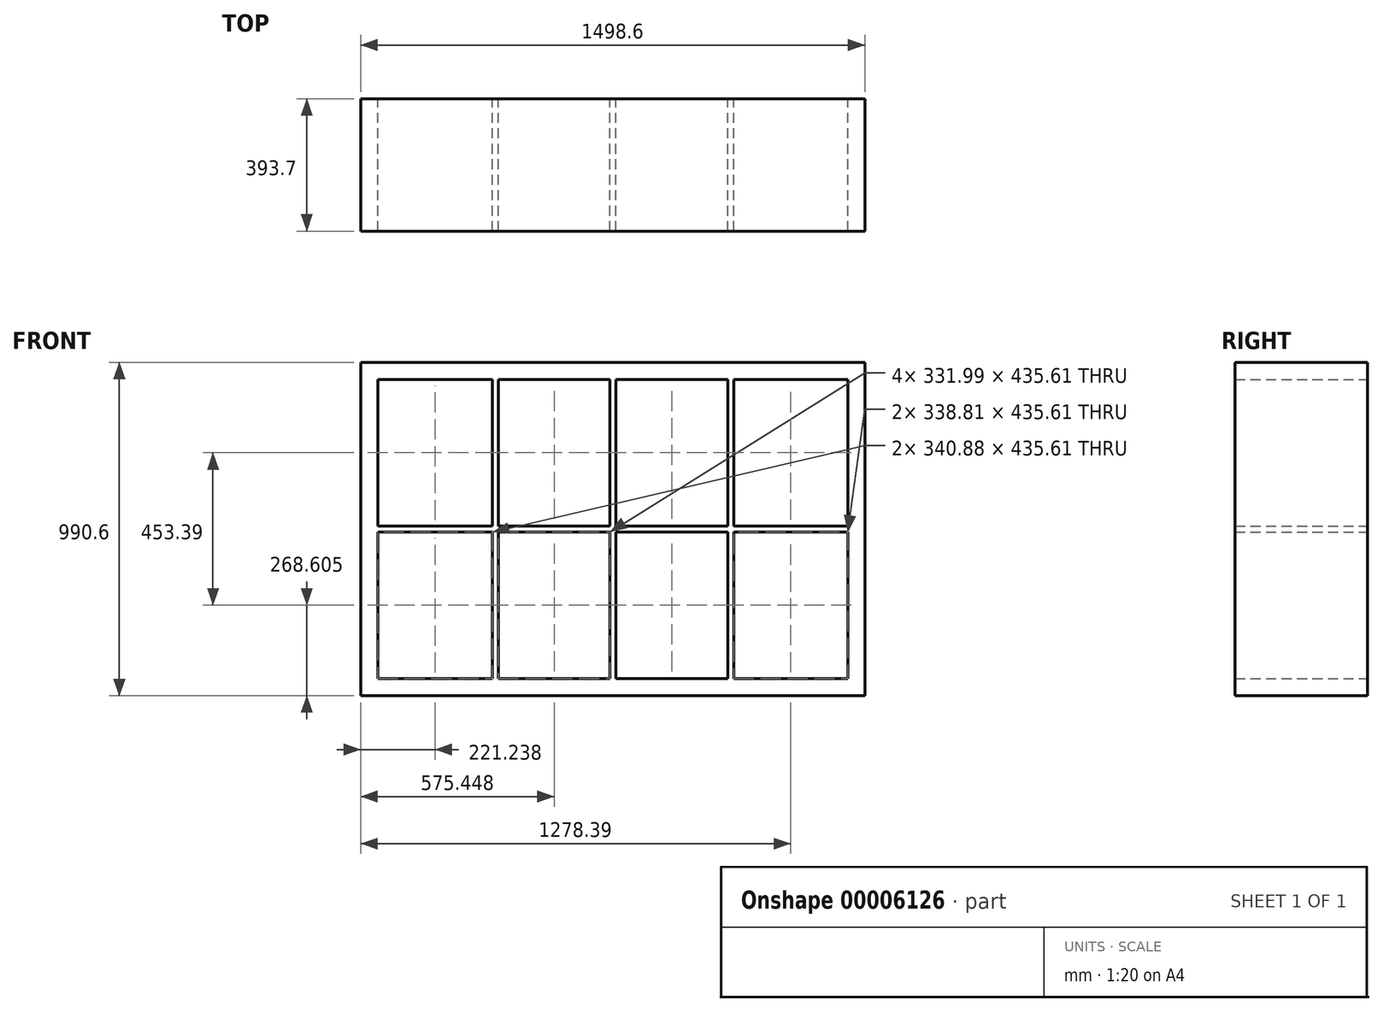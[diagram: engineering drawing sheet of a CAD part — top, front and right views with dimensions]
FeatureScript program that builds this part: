
annotation { "Feature Type Name" : "Feature", "Feature Type Description" : "" }
export const myFeature = defineFeature(function(context is Context, id is Id, definition is map)
    precondition{}
    {
        {
            var Q0;
            Q0=qCreatedBy(makeId("Front.planeOp"),FACE);
            var sketch = newSketch(context, id + "F0", { "sketchPlane" : qUnion([Q0])});
            skLineSegment(sketch, "E0.bottom", {"start": v(0, 0) * mm, "end": v(1498.6, 0) * mm});
            skLineSegment(sketch, "E0.top", {"start": v(0, 990.6) * mm, "end": v(1498.6, 990.6) * mm});
            skLineSegment(sketch, "E0.left", {"start": v(0, 0) * mm, "end": v(0, 990.6) * mm});
            skLineSegment(sketch, "E0.right", {"start": v(1498.6, 0) * mm, "end": v(1498.6, 990.6) * mm});
            skLineSegment(sketch, "E1.0", {"start": v(50.8, 50.8) * mm, "end": v(50.8, 939.8) * mm});
            skLineSegment(sketch, "E1.1", {"start": v(50.8, 50.8) * mm, "end": v(1447.8, 50.8) * mm});
            skLineSegment(sketch, "E1.2", {"start": v(1447.8, 50.8) * mm, "end": v(1447.8, 939.8) * mm});
            skLineSegment(sketch, "E1.3", {"start": v(50.8, 939.8) * mm, "end": v(1447.8, 939.8) * mm});
            skLineSegment(sketch, "E2", {"start": v(50.8, 495.3) * mm, "end": v(1447.8, 495.3) * mm, "construction": true});
            skLineSegment(sketch, "E3.1.0.0", {"start": v(400.57, 50.8) * mm, "end": v(400.57, 939.8) * mm, "construction": true});
            skLineSegment(sketch, "E3.2.0.0", {"start": v(750.33, 50.8) * mm, "end": v(750.33, 939.8) * mm, "construction": true});
            skLineSegment(sketch, "E3.3.0.0", {"start": v(1100.1, 50.8) * mm, "end": v(1100.1, 939.8) * mm, "construction": true});
            skLineSegment(sketch, "E3.4.0.0", {"start": v(1449.86, 50.8) * mm, "end": v(1449.86, 939.8) * mm});
            skLineSegment(sketch, "E3.direction1", {"start": v(50.8, 50.8) * mm, "end": v(400.57, 50.8) * mm, "construction": true});
            skLineSegment(sketch, "E4.0", {"start": v(409.46, 50.8) * mm, "end": v(409.46, 939.8) * mm});
            skLineSegment(sketch, "E5.0.MirrorCS", {"start": v(391.68, 50.8) * mm, "end": v(391.68, 939.8) * mm});
            skLineSegment(sketch, "E6.0", {"start": v(50.8, 486.41) * mm, "end": v(1447.8, 486.41) * mm});
            skLineSegment(sketch, "E7.0.MirrorCS", {"start": v(50.8, 504.2) * mm, "end": v(1447.8, 504.2) * mm});
            skLineSegment(sketch, "E8.0", {"start": v(759.22, 50.8) * mm, "end": v(759.22, 939.8) * mm});
            skLineSegment(sketch, "E9.0.MirrorCS", {"start": v(741.44, 50.8) * mm, "end": v(741.44, 939.8) * mm});
            skLineSegment(sketch, "E10.0", {"start": v(1108.99, 50.8) * mm, "end": v(1108.99, 939.8) * mm});
            skLineSegment(sketch, "E11.0.MirrorCS", {"start": v(1091.2, 50.8) * mm, "end": v(1091.2, 939.8) * mm});
            skSolve(sketch);
        }
        {
            var Q0;
            Q0=makeQuery(id+"F0.imprint","IMPRINT",FACE,{"disambiguationData":[TD([[makeQuery(id+"F0.imprint","IMPRINT",EDGE,{"derivedFrom":sQuery(id+"F0.wireOp",EDGE,"E0.bottom")}),1.0]])]});
            extrude(context, id + "F1", {"entities" : qUnion([Q0]), "depth" : 393.7 * mm});
        }
        {
            var Q0;
            {var subQ3=sQuery(id+"F0.wireOp",EDGE,"E1.0");var subQ5=sQuery(id+"F0.wireOp",EDGE,"E6.0");var subQ7=makeQuery(id+"F0.imprint","INTERSECT",VERTEX,{"derivedFrom":[subQ3,subQ5]});Q0=makeQuery(id+"F0.imprint","IMPRINT",FACE,{"disambiguationData":[TD([[makeQuery(id+"F0.imprint","IMPRINT",EDGE,{"disambiguationData":[TD([[subQ7,-1.0]])],"derivedFrom":subQ3}),-1.0]])]});}
            var Q1;
            {var subQ3=sQuery(id+"F0.wireOp",EDGE,"E1.1");var subQ5=sQuery(id+"F0.wireOp",EDGE,"E4.0");var subQ7=makeQuery(id+"F0.imprint","INTERSECT",VERTEX,{"derivedFrom":[subQ3,subQ5]});Q1=makeQuery(id+"F0.imprint","IMPRINT",FACE,{"disambiguationData":[TD([[makeQuery(id+"F0.imprint","IMPRINT",EDGE,{"disambiguationData":[TD([[subQ7,1.0]])],"derivedFrom":subQ3}),1.0]])]});}
            var Q2;
            {var subQ3=sQuery(id+"F0.wireOp",EDGE,"E4.0");var subQ5=sQuery(id+"F0.wireOp",EDGE,"E6.0");var subQ7=makeQuery(id+"F0.imprint","INTERSECT",VERTEX,{"derivedFrom":[subQ3,subQ5]});Q2=makeQuery(id+"F0.imprint","IMPRINT",FACE,{"disambiguationData":[TD([[makeQuery(id+"F0.imprint","IMPRINT",EDGE,{"disambiguationData":[TD([[subQ7,-1.0]])],"derivedFrom":subQ3}),-1.0]])]});}
            var Q3;
            {var subQ3=sQuery(id+"F0.wireOp",EDGE,"E4.0");var subQ5=sQuery(id+"F0.wireOp",EDGE,"E6.0");var subQ7=makeQuery(id+"F0.imprint","INTERSECT",VERTEX,{"derivedFrom":[subQ3,subQ5]});Q3=makeQuery(id+"F0.imprint","IMPRINT",FACE,{"disambiguationData":[TD([[makeQuery(id+"F0.imprint","IMPRINT",EDGE,{"disambiguationData":[TD([[subQ7,-1.0]])],"derivedFrom":subQ3}),1.0]])]});}
            var Q4;
            {var subQ3=sQuery(id+"F0.wireOp",EDGE,"E4.0");var subQ5=sQuery(id+"F0.wireOp",EDGE,"E1.3");var subQ7=makeQuery(id+"F0.imprint","INTERSECT",VERTEX,{"derivedFrom":[subQ5,subQ3]});Q4=makeQuery(id+"F0.imprint","IMPRINT",FACE,{"disambiguationData":[TD([[makeQuery(id+"F0.imprint","IMPRINT",EDGE,{"disambiguationData":[TD([[subQ7,1.0]])],"derivedFrom":subQ5}),-1.0]])]});}
            var Q5;
            {var subQ3=sQuery(id+"F0.wireOp",EDGE,"E1.3");var subQ5=sQuery(id+"F0.wireOp",EDGE,"E8.0");var subQ7=makeQuery(id+"F0.imprint","INTERSECT",VERTEX,{"derivedFrom":[subQ3,subQ5]});Q5=makeQuery(id+"F0.imprint","IMPRINT",FACE,{"disambiguationData":[TD([[makeQuery(id+"F0.imprint","IMPRINT",EDGE,{"disambiguationData":[TD([[subQ7,1.0]])],"derivedFrom":subQ3}),-1.0]])]});}
            var Q6;
            {var subQ0=sQuery(id+"F0.wireOp",EDGE,"E9.0.MirrorCS");var subQ3=sQuery(id+"F0.wireOp",EDGE,"E6.0");var subQ4=makeQuery(id+"F0.imprint","INTERSECT",VERTEX,{"derivedFrom":[subQ3,subQ0]});Q6=makeQuery(id+"F0.imprint","IMPRINT",FACE,{"disambiguationData":[TD([[makeQuery(id+"F0.imprint","IMPRINT",EDGE,{"disambiguationData":[TD([[subQ4,-1.0]])],"derivedFrom":subQ3}),1.0]])]});}
            var Q7;
            {var subQ3=sQuery(id+"F0.wireOp",EDGE,"E1.1");var subQ5=sQuery(id+"F0.wireOp",EDGE,"E8.0");var subQ7=makeQuery(id+"F0.imprint","INTERSECT",VERTEX,{"derivedFrom":[subQ3,subQ5]});Q7=makeQuery(id+"F0.imprint","IMPRINT",FACE,{"disambiguationData":[TD([[makeQuery(id+"F0.imprint","IMPRINT",EDGE,{"disambiguationData":[TD([[subQ7,1.0]])],"derivedFrom":subQ3}),1.0]])]});}
            var Q8;
            {var subQ3=sQuery(id+"F0.wireOp",EDGE,"E6.0");var subQ5=sQuery(id+"F0.wireOp",EDGE,"E8.0");var subQ7=makeQuery(id+"F0.imprint","INTERSECT",VERTEX,{"derivedFrom":[subQ3,subQ5]});Q8=makeQuery(id+"F0.imprint","IMPRINT",FACE,{"disambiguationData":[TD([[makeQuery(id+"F0.imprint","IMPRINT",EDGE,{"disambiguationData":[TD([[subQ7,-1.0]])],"derivedFrom":subQ3}),1.0]])]});}
            var Q9;
            {var subQ3=sQuery(id+"F0.wireOp",EDGE,"E1.3");var subQ5=sQuery(id+"F0.wireOp",EDGE,"E10.0");var subQ7=makeQuery(id+"F0.imprint","INTERSECT",VERTEX,{"derivedFrom":[subQ3,subQ5]});Q9=makeQuery(id+"F0.imprint","IMPRINT",FACE,{"disambiguationData":[TD([[makeQuery(id+"F0.imprint","IMPRINT",EDGE,{"disambiguationData":[TD([[subQ7,1.0]])],"derivedFrom":subQ3}),-1.0]])]});}
            var Q10;
            {var subQ3=sQuery(id+"F0.wireOp",EDGE,"E1.1");var subQ5=sQuery(id+"F0.wireOp",EDGE,"E10.0");var subQ7=makeQuery(id+"F0.imprint","INTERSECT",VERTEX,{"derivedFrom":[subQ3,subQ5]});Q10=makeQuery(id+"F0.imprint","IMPRINT",FACE,{"disambiguationData":[TD([[makeQuery(id+"F0.imprint","IMPRINT",EDGE,{"disambiguationData":[TD([[subQ7,1.0]])],"derivedFrom":subQ3}),1.0]])]});}
            var Q11;
            {var subQ3=sQuery(id+"F0.wireOp",EDGE,"E6.0");var subQ5=sQuery(id+"F0.wireOp",EDGE,"E1.2");var subQ7=makeQuery(id+"F0.imprint","INTERSECT",VERTEX,{"derivedFrom":[subQ5,subQ3]});Q11=makeQuery(id+"F0.imprint","IMPRINT",FACE,{"disambiguationData":[TD([[makeQuery(id+"F0.imprint","IMPRINT",EDGE,{"disambiguationData":[TD([[subQ7,-1.0]])],"derivedFrom":subQ5}),1.0]])]});}
            var Q12;
            {var subQ0=sQuery(id+"F0.wireOp",EDGE,"E11.0.MirrorCS");var subQ3=sQuery(id+"F0.wireOp",EDGE,"E6.0");var subQ4=makeQuery(id+"F0.imprint","INTERSECT",VERTEX,{"derivedFrom":[subQ3,subQ0]});Q12=makeQuery(id+"F0.imprint","IMPRINT",FACE,{"disambiguationData":[TD([[makeQuery(id+"F0.imprint","IMPRINT",EDGE,{"disambiguationData":[TD([[subQ4,-1.0]])],"derivedFrom":subQ3}),1.0]])]});}
            extrude(context, id + "F2", {"entities" : qUnion([Q0, Q1, Q2, Q3, Q4, Q5, Q6, Q7, Q8, Q9, Q10, Q11, Q12]), "operationType" : NewBodyOperationType.ADD, "depth" : 393.7 * mm});
        }
    });
